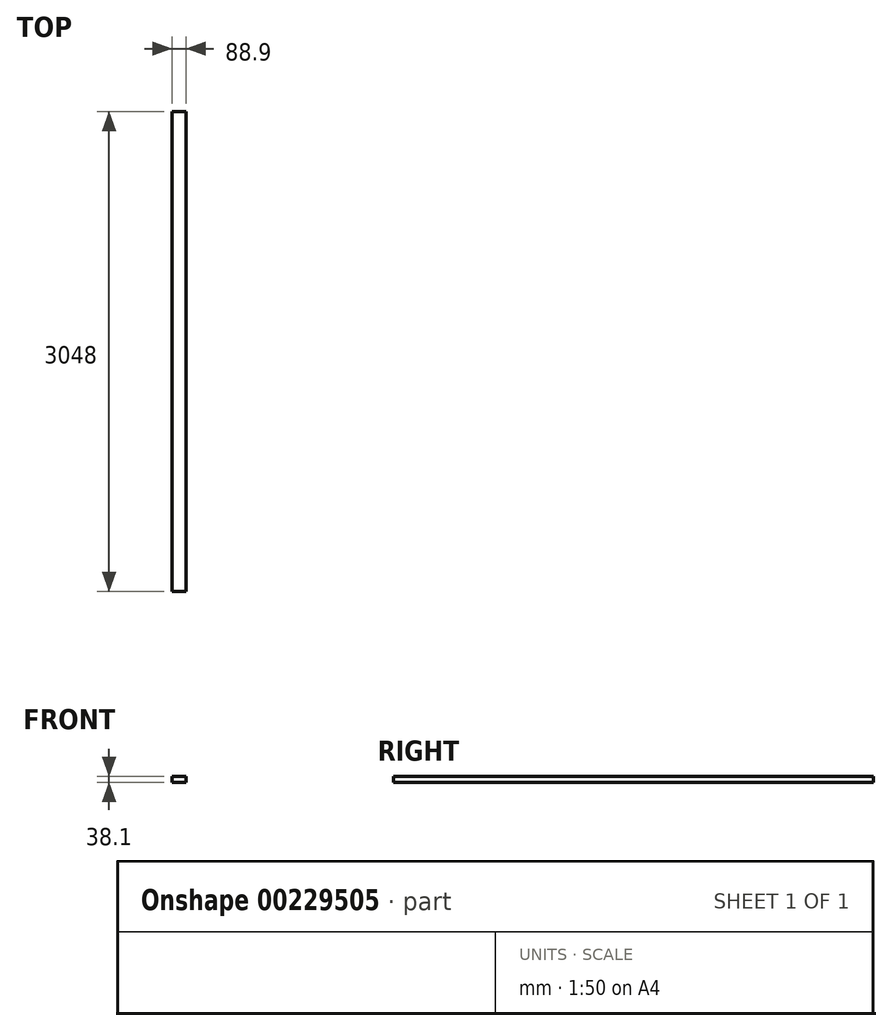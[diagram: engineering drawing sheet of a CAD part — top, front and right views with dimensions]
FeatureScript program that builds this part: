
annotation { "Feature Type Name" : "Feature", "Feature Type Description" : "" }
export const myFeature = defineFeature(function(context is Context, id is Id, definition is map)
    precondition{}
    {
        {
            var Q0;
            Q0=qCreatedBy(makeId("Front.planeOp"),FACE);
            var sketch = newSketch(context, id + "F0", { "sketchPlane" : qUnion([Q0])});
            skLineSegment(sketch, "E0.bottom", {"start": v(0, 0) * mm, "end": v(88.9, 0) * mm});
            skLineSegment(sketch, "E0.top", {"start": v(0, -38.1) * mm, "end": v(88.9, -38.1) * mm});
            skLineSegment(sketch, "E0.left", {"start": v(0, 0) * mm, "end": v(0, -38.1) * mm});
            skLineSegment(sketch, "E0.right", {"start": v(88.9, 0) * mm, "end": v(88.9, -38.1) * mm});
            skSolve(sketch);
        }
        {
            var Q0;
            Q0=qSketchRegion(id+"F0",true);
            extrude(context, id + "F1", {"entities" : qUnion([Q0]), "depth" : 3048 * mm});
        }
    });
